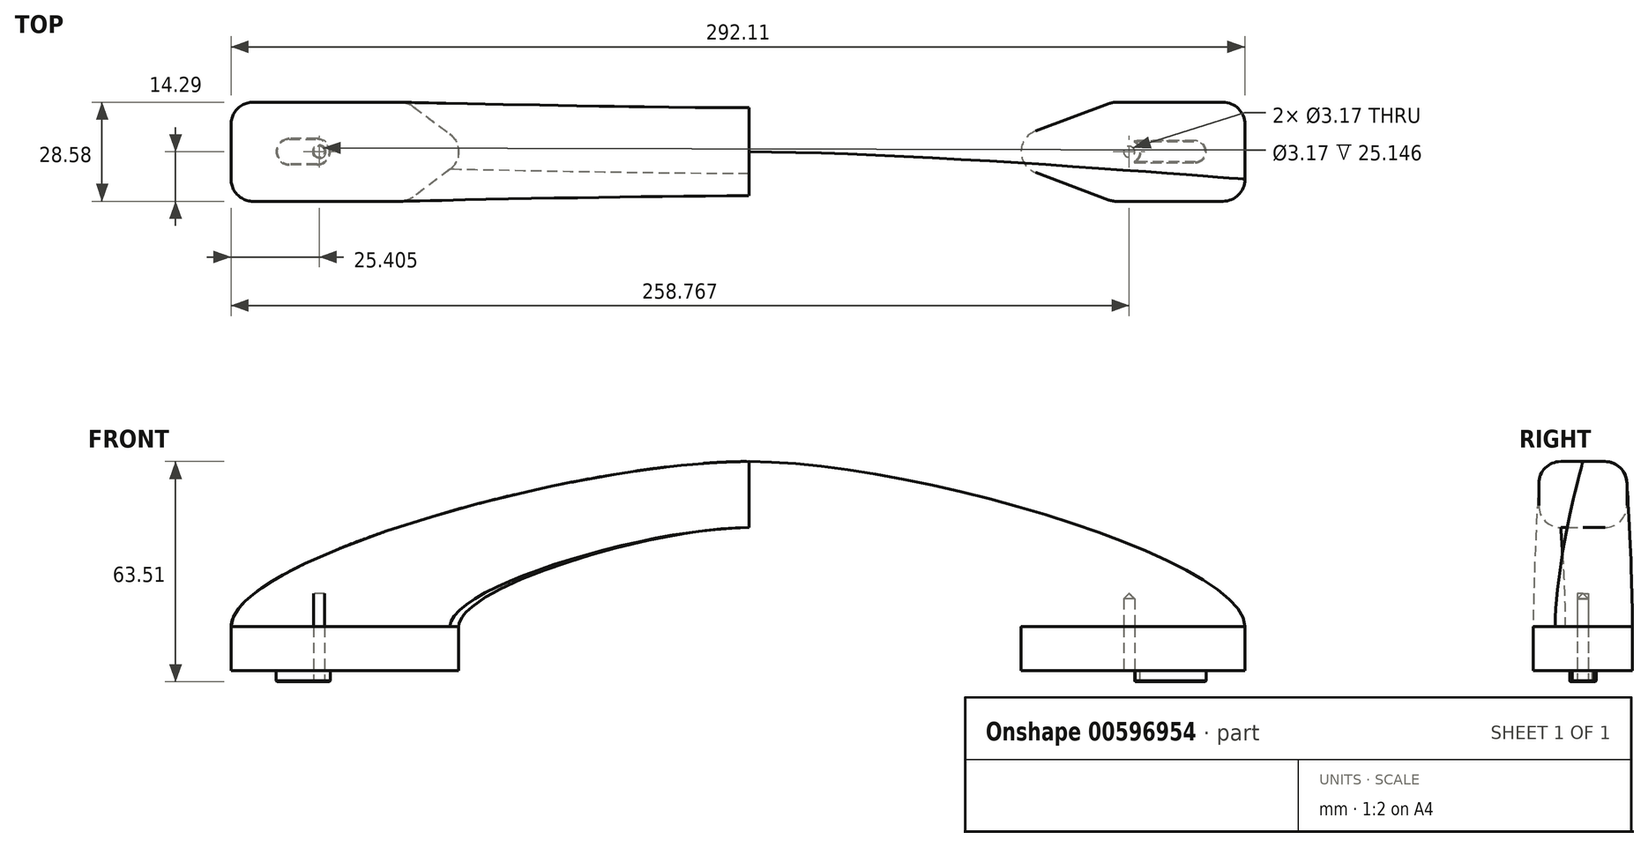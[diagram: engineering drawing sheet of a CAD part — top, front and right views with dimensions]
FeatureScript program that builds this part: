
annotation { "Feature Type Name" : "Feature", "Feature Type Description" : "" }
export const myFeature = defineFeature(function(context is Context, id is Id, definition is map)
    precondition{}
    {
        {
            var Q0;
            Q0=qCreatedBy(makeId("Top.planeOp"),FACE);
            var sketch = newSketch(context, id + "F0", { "sketchPlane" : qUnion([Q0])});
            skLineSegment(sketch, "E0.bottom", {"start": v(-100.54, -14.29) * mm, "end": v(-142.88, -14.29) * mm});
            skLineSegment(sketch, "E0.top", {"start": v(-100.54, 14.29) * mm, "end": v(-142.88, 14.29) * mm});
            skLineSegment(sketch, "E0.left", {"start": v(-98.42, -14.29) * mm, "end": v(-98.42, 14.29) * mm, "construction": true});
            skLineSegment(sketch, "E0.right", {"start": v(-149.23, -7.94) * mm, "end": v(-149.23, 7.94) * mm});
            skPoint(sketch, "E0.middle", {"position": v(-123.83, 0) * mm});
            skLineSegment(sketch, "E1", {"start": v(0, 0) * mm, "end": v(0, 50.83) * mm, "construction": true});
            skLineSegment(sketch, "E2.bottom", {"start": v(136.53, -14.29) * mm, "end": v(105.93, -14.29) * mm, "construction": true});
            skLineSegment(sketch, "E2.top", {"start": v(136.53, 14.29) * mm, "end": v(105.93, 14.29) * mm, "construction": true});
            skLineSegment(sketch, "E2.left", {"start": v(142.88, -7.94) * mm, "end": v(142.88, 7.94) * mm, "construction": true});
            skLineSegment(sketch, "E2.right", {"start": v(104.78, -14.29) * mm, "end": v(104.78, 14.29) * mm, "construction": true});
            skPoint(sketch, "E2.middle", {"position": v(123.83, 0) * mm});
            skLineSegment(sketch, "E3", {"start": v(103.7, 13.88) * mm, "end": v(82.53, 5.95) * mm, "construction": true});
            skLineSegment(sketch, "E4", {"start": v(82.53, -5.95) * mm, "end": v(103.7, -13.88) * mm, "construction": true});
            skPoint(sketch, "E5.visualSharp", {"position": v(66.68, 0) * mm});
            skArc(sketch, "E5.filletArc", {"start": v(82.53, 5.95) * mm, "mid": v(78.4, 0) * mm, "end": v(82.53, -5.95) * mm, "construction": true});
            skLineSegment(sketch, "E6", {"start": v(-96.73, 13.02) * mm, "end": v(-86.15, 5.08) * mm});
            skLineSegment(sketch, "E7", {"start": v(-86.15, -5.08) * mm, "end": v(-96.73, -13.02) * mm});
            skPoint(sketch, "E8.visualSharp", {"position": v(-79.38, 0) * mm});
            skArc(sketch, "E8.filletArc", {"start": v(-86.15, -5.08) * mm, "mid": v(-83.6, 0) * mm, "end": v(-86.15, 5.08) * mm});
            skPoint(sketch, "E9.visualSharp", {"position": v(-149.23, 14.29) * mm});
            skArc(sketch, "E9.filletArc", {"start": v(-142.88, 14.29) * mm, "mid": v(-147.37, 12.43) * mm, "end": v(-149.23, 7.94) * mm});
            skPoint(sketch, "E10.visualSharp", {"position": v(-149.23, -14.29) * mm});
            skArc(sketch, "E10.filletArc", {"start": v(-149.23, -7.94) * mm, "mid": v(-147.37, -12.43) * mm, "end": v(-142.88, -14.29) * mm});
            skPoint(sketch, "E11.visualSharp", {"position": v(142.88, 14.29) * mm});
            skArc(sketch, "E11.filletArc", {"start": v(142.88, 7.94) * mm, "mid": v(141.02, 12.43) * mm, "end": v(136.53, 14.29) * mm, "construction": true});
            skPoint(sketch, "E12.visualSharp", {"position": v(142.88, -14.29) * mm});
            skArc(sketch, "E12.filletArc", {"start": v(136.53, -14.29) * mm, "mid": v(141.02, -12.43) * mm, "end": v(142.88, -7.94) * mm, "construction": true});
            skPoint(sketch, "E13.visualSharp", {"position": v(104.78, -14.29) * mm});
            skArc(sketch, "E13.filletArc", {"start": v(103.7, -13.88) * mm, "mid": v(104.8, -14.19) * mm, "end": v(105.93, -14.29) * mm});
            skPoint(sketch, "E14.visualSharp", {"position": v(104.78, 14.29) * mm});
            skArc(sketch, "E14.filletArc", {"start": v(105.93, 14.29) * mm, "mid": v(104.8, 14.19) * mm, "end": v(103.7, 13.88) * mm, "construction": true});
            skPoint(sketch, "E15.visualSharp", {"position": v(-98.43, 14.29) * mm});
            skArc(sketch, "E15.filletArc", {"start": v(-96.73, 13.02) * mm, "mid": v(-98.53, 13.96) * mm, "end": v(-100.54, 14.29) * mm});
            skPoint(sketch, "E16.visualSharp", {"position": v(-98.43, -14.29) * mm});
            skArc(sketch, "E16.filletArc", {"start": v(-100.54, -14.29) * mm, "mid": v(-98.53, -13.96) * mm, "end": v(-96.73, -13.02) * mm});
            skSolve(sketch);
        }
        {
            var Q0;
            Q0=qCreatedBy(makeId("Front.planeOp"),FACE);
            var sketch = newSketch(context, id + "F1", { "sketchPlane" : qUnion([Q0])});
            skLineSegment(sketch, "E17", {"start": v(-123.83, 0) * mm, "end": v(-123.83, 25.4) * mm});
            skLineSegment(sketch, "E18", {"start": v(0, 0) * mm, "end": v(0, 50.8) * mm, "construction": true});
            skPoint(sketch, "E19.start.orphan", {"position": v(123.83, 0) * mm});
            skArc(sketch, "E20", {"start": v(0, 50.8) * mm, "mid": v(-62.89, 42.84) * mm, "end": v(-123.82, 25.4) * mm});
            skSolve(sketch);
        }
        {
            var Q0;
            Q0=qCreatedBy(makeId("Top.planeOp"),FACE);
            var sketch = newSketch(context, id + "F2", { "sketchPlane" : qUnion([Q0])});
            skLineSegment(sketch, "E21.0", {"start": v(103.7, 13.88) * mm, "end": v(82.53, 5.95) * mm});
            skArc(sketch, "E21.1", {"start": v(105.93, 14.29) * mm, "mid": v(104.8, 14.19) * mm, "end": v(103.7, 13.88) * mm});
            skLineSegment(sketch, "E21.2", {"start": v(136.53, 14.29) * mm, "end": v(105.93, 14.29) * mm});
            skLineSegment(sketch, "E21.3", {"start": v(104.78, -14.29) * mm, "end": v(104.78, 14.29) * mm, "construction": true});
            skArc(sketch, "E21.4", {"start": v(103.7, -13.88) * mm, "mid": v(104.8, -14.19) * mm, "end": v(105.93, -14.29) * mm});
            skLineSegment(sketch, "E21.5", {"start": v(82.53, -5.95) * mm, "end": v(103.7, -13.88) * mm});
            skLineSegment(sketch, "E21.6", {"start": v(136.53, -14.29) * mm, "end": v(105.93, -14.29) * mm});
            skArc(sketch, "E21.7", {"start": v(82.53, 5.95) * mm, "mid": v(78.4, 0) * mm, "end": v(82.53, -5.95) * mm});
            skArc(sketch, "E21.8", {"start": v(142.88, 7.94) * mm, "mid": v(141.02, 12.43) * mm, "end": v(136.53, 14.29) * mm});
            skArc(sketch, "E21.9", {"start": v(136.53, -14.29) * mm, "mid": v(141.02, -12.43) * mm, "end": v(142.88, -7.94) * mm});
            skLineSegment(sketch, "E21.10", {"start": v(142.88, -7.94) * mm, "end": v(142.88, 7.94) * mm});
            skSolve(sketch);
        }
        {
            var Q0;
            Q0=qCreatedBy(makeId("Front.planeOp"),FACE);
            var sketch = newSketch(context, id + "F3", { "sketchPlane" : qUnion([Q0])});
            skLineSegment(sketch, "E22.1", {"start": v(-123.83, 0) * mm, "end": v(-123.83, 25.4) * mm});
            skLineSegment(sketch, "E23.MirrorCS", {"start": v(123.83, 0) * mm, "end": v(123.83, 25.4) * mm});
            skArc(sketch, "E24", {"start": v(123.83, 25.4) * mm, "mid": v(0, 50.8) * mm, "end": v(-123.83, 25.4) * mm});
            skSolve(sketch);
        }
        {
            var Q0;
            Q0=makeQuery(id+"F0.imprint","IMPRINT",FACE,{"disambiguationData":[TD([[makeQuery(id+"F0.imprint","IMPRINT",EDGE,{"derivedFrom":sQuery(id+"F0.wireOp",EDGE,"E0.bottom")}),-1.0]])]});
            extrude(context, id + "F4", {"entities" : qUnion([Q0]), "depth" : 12.7 * mm, "offsetDistance" : 25.4 * mm});
        }
        {
            var Q0;
            Q0=makeQuery(id+"F2.imprint","IMPRINT",FACE,{"disambiguationData":[TD([[makeQuery(id+"F2.imprint","IMPRINT",EDGE,{"derivedFrom":sQuery(id+"F2.wireOp",EDGE,"E21.0")}),1.0]])]});
            extrude(context, id + "F5", {"entities" : qUnion([Q0]), "depth" : 12.7 * mm, "offsetDistance" : 25.4 * mm});
        }
        {
            var Q0;
            Q0=qCreatedBy(makeId("Right.planeOp"),FACE);
            var sketch = newSketch(context, id + "F6", { "sketchPlane" : qUnion([Q0])});
            skLineSegment(sketch, "E25.bottom", {"start": v(-6.35, 41.27) * mm, "end": v(6.35, 41.27) * mm});
            skLineSegment(sketch, "E25.top", {"start": v(-6.35, 60.32) * mm, "end": v(6.35, 60.32) * mm});
            skLineSegment(sketch, "E25.left", {"start": v(-12.7, 47.62) * mm, "end": v(-12.7, 53.97) * mm});
            skLineSegment(sketch, "E25.right", {"start": v(12.7, 47.62) * mm, "end": v(12.7, 53.97) * mm});
            skPoint(sketch, "E25.middle", {"position": v(0, 50.8) * mm});
            skPoint(sketch, "E26.visualSharp", {"position": v(12.7, 60.32) * mm});
            skArc(sketch, "E26.filletArc", {"start": v(12.7, 53.97) * mm, "mid": v(10.84, 58.47) * mm, "end": v(6.35, 60.32) * mm});
            skPoint(sketch, "E27.visualSharp", {"position": v(-12.7, 60.32) * mm});
            skArc(sketch, "E27.filletArc", {"start": v(-6.35, 60.32) * mm, "mid": v(-10.84, 58.47) * mm, "end": v(-12.7, 53.97) * mm});
            skPoint(sketch, "E28.visualSharp", {"position": v(-12.7, 41.27) * mm});
            skArc(sketch, "E28.filletArc", {"start": v(-12.7, 47.62) * mm, "mid": v(-10.84, 43.13) * mm, "end": v(-6.35, 41.27) * mm});
            skPoint(sketch, "E29.visualSharp", {"position": v(12.7, 41.27) * mm});
            skArc(sketch, "E29.filletArc", {"start": v(6.35, 41.27) * mm, "mid": v(10.84, 43.13) * mm, "end": v(12.7, 47.62) * mm});
            skSolve(sketch);
        }
        {
            var Q1;
            Q1=makeQuery(id+"F6.imprint","IMPRINT",FACE,{"disambiguationData":[TD([[makeQuery(id+"F6.imprint","IMPRINT",EDGE,{"derivedFrom":sQuery(id+"F6.wireOp",EDGE,"E25.bottom")}),1.0]])]});
            var Q2;
            Q2=makeQuery(id+"F4.opExtrude","CAP_FACE",FACE,{"disambiguationData":[OSD([sQuery(id+"F0.wireOp",EDGE,"E0.bottom"),sQuery(id+"F0.wireOp",EDGE,"E0.top"),sQuery(id+"F0.wireOp",EDGE,"E0.right"),sQuery(id+"F0.wireOp",EDGE,"E6"),sQuery(id+"F0.wireOp",EDGE,"E7"),sQuery(id+"F0.wireOp",EDGE,"E8.filletArc"),sQuery(id+"F0.wireOp",EDGE,"E9.filletArc"),sQuery(id+"F0.wireOp",EDGE,"E10.filletArc"),sQuery(id+"F0.wireOp",EDGE,"E15.filletArc"),sQuery(id+"F0.wireOp",EDGE,"E16.filletArc")])],"isStart":false});
            var Q3;
            Q3=sQuery(id+"F3.wireOp",EDGE,"E22.0");
            var Q4;
            Q4=sQuery(id+"F6.wireOp",VERTEX,"E25.middle");
            var Q5;
            Q5=sQuery(id+"F3.wireOp",VERTEX,"E22.1.end");
            loft(context, id + "F7", {"operationType" : NewBodyOperationType.ADD, "startCondition" : LoftEndDerivativeType.NORMAL_TO_PROFILE, "startMagnitude" : 1, "endCondition" : LoftEndDerivativeType.NORMAL_TO_PROFILE, "endMagnitude" : 1, "sheetProfilesArray" : [{ "sheetProfileEntities" : qUnion([Q1]) }, { "sheetProfileEntities" : qUnion([Q2]) }], "guidesArray" : [{ "guideEntities" : qUnion([Q3]), "guideDerivativeType" : LoftGuideDerivativeType.DEFAULT, "guideDerivativeMagnitude" : 1 }], "connections" : [{ "connectionEntities" : qUnion([Q4, Q5]), "connectionEdgeQueries" : qUnion([]), "connectionEdgeParameters" : [] }]});
        }
        {
            var Q0;
            Q0=makeQuery(id+"F7.opLoft","CAP_FACE",FACE,{"disambiguationData":[OSD([makeQuery(id+"F6.imprint","IMPRINT",FACE,{"disambiguationData":[TD([[makeQuery(id+"F6.imprint","IMPRINT",EDGE,{"derivedFrom":sQuery(id+"F6.wireOp",EDGE,"E25.bottom")}),1.0]])]})])],"isStart":true});
            var Q1;
            Q1=makeQuery(id+"F5.opExtrude","CAP_FACE",FACE,{"disambiguationData":[OSD([sQuery(id+"F2.wireOp",EDGE,"E21.0"),sQuery(id+"F2.wireOp",EDGE,"E21.1"),sQuery(id+"F2.wireOp",EDGE,"E21.2"),sQuery(id+"F2.wireOp",EDGE,"E21.4"),sQuery(id+"F2.wireOp",EDGE,"E21.5"),sQuery(id+"F2.wireOp",EDGE,"E21.6"),sQuery(id+"F2.wireOp",EDGE,"E21.7"),sQuery(id+"F2.wireOp",EDGE,"E21.8"),sQuery(id+"F2.wireOp",EDGE,"E21.9"),sQuery(id+"F2.wireOp",EDGE,"E21.10")])],"isStart":false});
            loft(context, id + "F8", {"startCondition" : LoftEndDerivativeType.NORMAL_TO_PROFILE, "startMagnitude" : 1, "endCondition" : LoftEndDerivativeType.NORMAL_TO_PROFILE, "endMagnitude" : 1, "sheetProfilesArray" : [{ "sheetProfileEntities" : qUnion([Q0]) }, { "sheetProfileEntities" : qUnion([Q1]) }]});
        }
        {
            var Q0;
            Q0=makeQuery(id+"F2.imprint","IMPRINT",FACE,{"disambiguationData":[TD([[makeQuery(id+"F2.imprint","IMPRINT",EDGE,{"derivedFrom":sQuery(id+"F2.wireOp",EDGE,"E21.0")}),1.0]])]});
            var sketch = newSketch(context, id + "F9", { "sketchPlane" : qUnion([Q0])});
            skCircle(sketch, "E30", {"center": v(109.54, 0) * mm, "radius": 1.59 * mm});
            skCircle(sketch, "E31", {"center": v(-123.83, 0) * mm, "radius": 1.59 * mm});
            skSolve(sketch);
        }
        {
            var Q0;
            Q0=makeQuery(id+"F9.imprint","IMPRINT",FACE,{"disambiguationData":[TD([[makeQuery(id+"F9.imprint","IMPRINT",EDGE,{"derivedFrom":sQuery(id+"F9.wireOp",EDGE,"E31")}),1.0]])]});
            var Q1;
            Q1=makeQuery(id+"F9.imprint","IMPRINT",FACE,{"disambiguationData":[TD([[makeQuery(id+"F9.imprint","IMPRINT",EDGE,{"derivedFrom":sQuery(id+"F9.wireOp",EDGE,"E30")}),1.0]])]});
            extrude(context, id + "F10", {"entities" : qUnion([Q0, Q1]), "operationType" : NewBodyOperationType.REMOVE, "depth" : 22.22 * mm, "offsetDistance" : 25.4 * mm});
        }
        {
            var Q0;
            Q0=makeQuery(id+"F4.opExtrude","CAP_FACE",FACE,{"disambiguationData":[OSD([sQuery(id+"F0.wireOp",EDGE,"E0.bottom"),sQuery(id+"F0.wireOp",EDGE,"E0.top"),sQuery(id+"F0.wireOp",EDGE,"E0.right"),sQuery(id+"F0.wireOp",EDGE,"E6"),sQuery(id+"F0.wireOp",EDGE,"E7"),sQuery(id+"F0.wireOp",EDGE,"E8.filletArc"),sQuery(id+"F0.wireOp",EDGE,"E9.filletArc"),sQuery(id+"F0.wireOp",EDGE,"E10.filletArc"),sQuery(id+"F0.wireOp",EDGE,"E15.filletArc"),sQuery(id+"F0.wireOp",EDGE,"E16.filletArc")])],"isStart":true});
            var sketch = newSketch(context, id + "F11", { "sketchPlane" : qUnion([Q0])});
            skLineSegment(sketch, "E32", {"start": v(-123.83, 0) * mm, "end": v(-136.2, 0) * mm, "construction": true});
            skLineSegment(sketch, "E33.0", {"start": v(-124.46, -3.8) * mm, "end": v(-132.4, -3.81) * mm});
            skLineSegment(sketch, "E34.0", {"start": v(-124.46, 3.81) * mm, "end": v(-132.4, 3.8) * mm});
            skArc(sketch, "E35", {"start": v(-132.4, 3.8) * mm, "mid": v(-136.2, 0) * mm, "end": v(-132.4, -3.81) * mm});
            skArc(sketch, "E36", {"start": v(-124.46, -3.8) * mm, "mid": v(-120.65, 0) * mm, "end": v(-124.46, 3.8) * mm});
            skSolve(sketch);
        }
        {
            var Q0;
            Q0=makeQuery(id+"F11.imprint","IMPRINT",FACE,{"disambiguationData":[TD([[makeQuery(id+"F11.imprint","IMPRINT",EDGE,{"derivedFrom":sQuery(id+"F11.wireOp",EDGE,"E33.0")}),-1.0]])]});
            extrude(context, id + "F12", {"entities" : qUnion([Q0]), "operationType" : NewBodyOperationType.ADD, "depth" : 3.17 * mm, "offsetDistance" : 25.4 * mm});
        }
        {
            var Q0;
            Q0=makeQuery(id+"F2.imprint","IMPRINT",FACE,{"disambiguationData":[TD([[makeQuery(id+"F2.imprint","IMPRINT",EDGE,{"derivedFrom":sQuery(id+"F2.wireOp",EDGE,"E21.0")}),1.0]])]});
            var sketch = newSketch(context, id + "F13", { "sketchPlane" : qUnion([Q0])});
            skCircle(sketch, "E37.0", {"center": v(109.54, 0) * mm, "radius": 1.59 * mm, "construction": true});
            skArc(sketch, "E38", {"start": v(109.54, -3.18) * mm, "mid": v(112.71, 0) * mm, "end": v(109.54, 3.17) * mm});
            skLineSegment(sketch, "E39", {"start": v(106.36, 0) * mm, "end": v(131.76, 0) * mm, "construction": true});
            skLineSegment(sketch, "E40", {"start": v(109.54, 0) * mm, "end": v(109.54, -10.63) * mm, "construction": true});
            skLineSegment(sketch, "E41", {"start": v(128.59, -10.63) * mm, "end": v(128.59, 0) * mm, "construction": true});
            skLineSegment(sketch, "E42", {"start": v(109.54, -3.18) * mm, "end": v(128.59, -3.17) * mm});
            skPoint(sketch, "E42.startSnap0", {"position": v(109.54, -5.31) * mm});
            skLineSegment(sketch, "E43.MirrorCS", {"start": v(109.54, 3.18) * mm, "end": v(128.59, 3.17) * mm});
            skArc(sketch, "E44", {"start": v(125.41, 0) * mm, "mid": v(126.34, -2.25) * mm, "end": v(128.59, -3.17) * mm, "construction": true});
            skArc(sketch, "E45", {"start": v(128.59, -3.17) * mm, "mid": v(131.76, 0) * mm, "end": v(128.59, 3.18) * mm});
            skArc(sketch, "E46", {"start": v(128.59, 3.18) * mm, "mid": v(126.34, 2.25) * mm, "end": v(125.41, 0) * mm, "construction": true});
            skSolve(sketch);
        }
        {
            var Q0;
            Q0=qSketchRegion(id+"F13",true);
            extrude(context, id + "F14", {"entities" : qUnion([Q0]), "operationType" : NewBodyOperationType.ADD, "oppositeDirection" : true, "depth" : 3.17 * mm, "offsetDistance" : 25.4 * mm});
        }
        {
            var Q0;
            Q0=makeQuery(id+"F12.opExtrude","CAP_EDGE",EDGE,{"disambiguationData":[OSD([sQuery(id+"F9.wireOp",EDGE,"E31")])],"isStart":false});
            chamfer(context, id + "F15", {"entities" : qUnion([Q0]), "width" : 0.25 * mm, "tangentPropagation" : true});
        }
        {
            var Q0;
            Q0=makeQuery(id+"F14.opExtrude","CAP_EDGE",EDGE,{"disambiguationData":[OSD([sQuery(id+"F13.wireOp",EDGE,"E38")])],"isStart":false});
            var Q1;
            Q1=makeQuery(id+"F14.opExtrude","CAP_FACE",FACE,{"disambiguationData":[OSD([sQuery(id+"F13.wireOp",EDGE,"E38"),sQuery(id+"F13.wireOp",EDGE,"E42"),sQuery(id+"F13.wireOp",EDGE,"E43.MirrorCS"),sQuery(id+"F13.wireOp",EDGE,"E45")])],"isStart":false});
            var Q2;
            Q2=makeQuery(id+"F14.opExtrude","SWEPT_EDGE",EDGE,{"disambiguationData":[OSD([sQuery(id+"F13.wireOp",EDGE,"E38"),sQuery(id+"F13.wireOp",EDGE,"E42")])]});
            var Q3;
            Q3=makeQuery(id+"F14.opExtrude","SWEPT_EDGE",EDGE,{"disambiguationData":[OSD([sQuery(id+"F13.wireOp",EDGE,"E38"),sQuery(id+"F13.wireOp",EDGE,"E43.MirrorCS")])]});
            var Q4;
            Q4=makeQuery(id+"F10.boolean.opBoolean","COPY",EDGE,{"derivedFrom":makeQuery(id+"F10.opExtrude","CAP_EDGE",EDGE,{"disambiguationData":[OSD([sQuery(id+"F9.wireOp",EDGE,"E30")])],"isStart":true})});
            chamfer(context, id + "F16", {"entities" : qUnion([Q0, Q1, Q2, Q3, Q4]), "width" : 0.25 * mm, "tangentPropagation" : true});
        }
        {
            var Q0;
            Q0=makeQuery(id+"F10.boolean.opBoolean","COPY",FACE,{"derivedFrom":makeQuery(id+"F10.opExtrude","CAP_FACE",FACE,{"disambiguationData":[OSD([sQuery(id+"F9.wireOp",EDGE,"E30")])],"isStart":false})});
            var Q1;
            Q1=makeQuery(id+"F10.opExtrude","CAP_FACE",FACE,{"disambiguationData":[OSD([sQuery(id+"F9.wireOp",EDGE,"E31")])],"isStart":false});
            chamfer(context, id + "F17", {"entities" : qUnion([Q0, Q1]), "width" : 1.52 * mm, "tangentPropagation" : true});
        }
        {
            var Q0;
            Q0=makeQuery(id+"F12.opExtrude","CAP_FACE",FACE,{"disambiguationData":[OSD([sQuery(id+"F9.wireOp",EDGE,"E31"),sQuery(id+"F11.wireOp",EDGE,"E33.0"),sQuery(id+"F11.wireOp",EDGE,"E34.0"),sQuery(id+"F11.wireOp",EDGE,"E35"),sQuery(id+"F11.wireOp",EDGE,"E36")])],"isStart":false});
            chamfer(context, id + "F18", {"entities" : qUnion([Q0]), "width" : 0.25 * mm, "tangentPropagation" : true});
        }
        {
            var Q0;
            Q0=makeQuery(id+"F14.opExtrude","CAP_EDGE",EDGE,{"disambiguationData":[OSD([sQuery(id+"F13.wireOp",EDGE,"E42")])],"isStart":true});
            var Q1;
            Q1=makeQuery(id+"F14.opExtrude","CAP_EDGE",EDGE,{"disambiguationData":[OSD([sQuery(id+"F13.wireOp",EDGE,"E38")])],"isStart":true});
            var Q2;
            Q2=makeQuery(id+"F16.opChamfer","BLEND_EDGE",EDGE,{"blendedFrom":[makeQuery(id+"F14.opExtrude","SWEPT_EDGE",EDGE,{"disambiguationData":[OSD([sQuery(id+"F13.wireOp",EDGE,"E38"),sQuery(id+"F13.wireOp",EDGE,"E42")])]}),makeQuery(id+"F5.opExtrude","CAP_FACE",FACE,{"disambiguationData":[OSD([sQuery(id+"F2.wireOp",EDGE,"E21.0"),sQuery(id+"F2.wireOp",EDGE,"E21.1"),sQuery(id+"F2.wireOp",EDGE,"E21.2"),sQuery(id+"F2.wireOp",EDGE,"E21.4"),sQuery(id+"F2.wireOp",EDGE,"E21.5"),sQuery(id+"F2.wireOp",EDGE,"E21.6"),sQuery(id+"F2.wireOp",EDGE,"E21.7"),sQuery(id+"F2.wireOp",EDGE,"E21.8"),sQuery(id+"F2.wireOp",EDGE,"E21.9"),sQuery(id+"F2.wireOp",EDGE,"E21.10")])],"isStart":true})],"blendedInto":[makeQuery(id+"F5.opExtrude","CAP_FACE",FACE,{"disambiguationData":[OSD([sQuery(id+"F2.wireOp",EDGE,"E21.0"),sQuery(id+"F2.wireOp",EDGE,"E21.1"),sQuery(id+"F2.wireOp",EDGE,"E21.2"),sQuery(id+"F2.wireOp",EDGE,"E21.4"),sQuery(id+"F2.wireOp",EDGE,"E21.5"),sQuery(id+"F2.wireOp",EDGE,"E21.6"),sQuery(id+"F2.wireOp",EDGE,"E21.7"),sQuery(id+"F2.wireOp",EDGE,"E21.8"),sQuery(id+"F2.wireOp",EDGE,"E21.9"),sQuery(id+"F2.wireOp",EDGE,"E21.10")])],"isStart":true})]});
            var Q3;
            Q3=makeQuery(id+"F16.opChamfer","BLEND_EDGE",EDGE,{"blendedFrom":[makeQuery(id+"F14.opExtrude","SWEPT_EDGE",EDGE,{"disambiguationData":[OSD([sQuery(id+"F13.wireOp",EDGE,"E38"),sQuery(id+"F13.wireOp",EDGE,"E43.MirrorCS")])]}),makeQuery(id+"F5.opExtrude","CAP_FACE",FACE,{"disambiguationData":[OSD([sQuery(id+"F2.wireOp",EDGE,"E21.0"),sQuery(id+"F2.wireOp",EDGE,"E21.1"),sQuery(id+"F2.wireOp",EDGE,"E21.2"),sQuery(id+"F2.wireOp",EDGE,"E21.4"),sQuery(id+"F2.wireOp",EDGE,"E21.5"),sQuery(id+"F2.wireOp",EDGE,"E21.6"),sQuery(id+"F2.wireOp",EDGE,"E21.7"),sQuery(id+"F2.wireOp",EDGE,"E21.8"),sQuery(id+"F2.wireOp",EDGE,"E21.9"),sQuery(id+"F2.wireOp",EDGE,"E21.10")])],"isStart":true})],"blendedInto":[makeQuery(id+"F5.opExtrude","CAP_FACE",FACE,{"disambiguationData":[OSD([sQuery(id+"F2.wireOp",EDGE,"E21.0"),sQuery(id+"F2.wireOp",EDGE,"E21.1"),sQuery(id+"F2.wireOp",EDGE,"E21.2"),sQuery(id+"F2.wireOp",EDGE,"E21.4"),sQuery(id+"F2.wireOp",EDGE,"E21.5"),sQuery(id+"F2.wireOp",EDGE,"E21.6"),sQuery(id+"F2.wireOp",EDGE,"E21.7"),sQuery(id+"F2.wireOp",EDGE,"E21.8"),sQuery(id+"F2.wireOp",EDGE,"E21.9"),sQuery(id+"F2.wireOp",EDGE,"E21.10")])],"isStart":true})]});
            var Q4;
            Q4=makeQuery(id+"F12.opExtrude","CAP_EDGE",EDGE,{"disambiguationData":[OSD([sQuery(id+"F11.wireOp",EDGE,"E33.0")])],"isStart":true});
            chamfer(context, id + "F19", {"entities" : qUnion([Q0, Q1, Q2, Q3, Q4]), "width" : 0.25 * mm, "tangentPropagation" : true});
        }
    });
